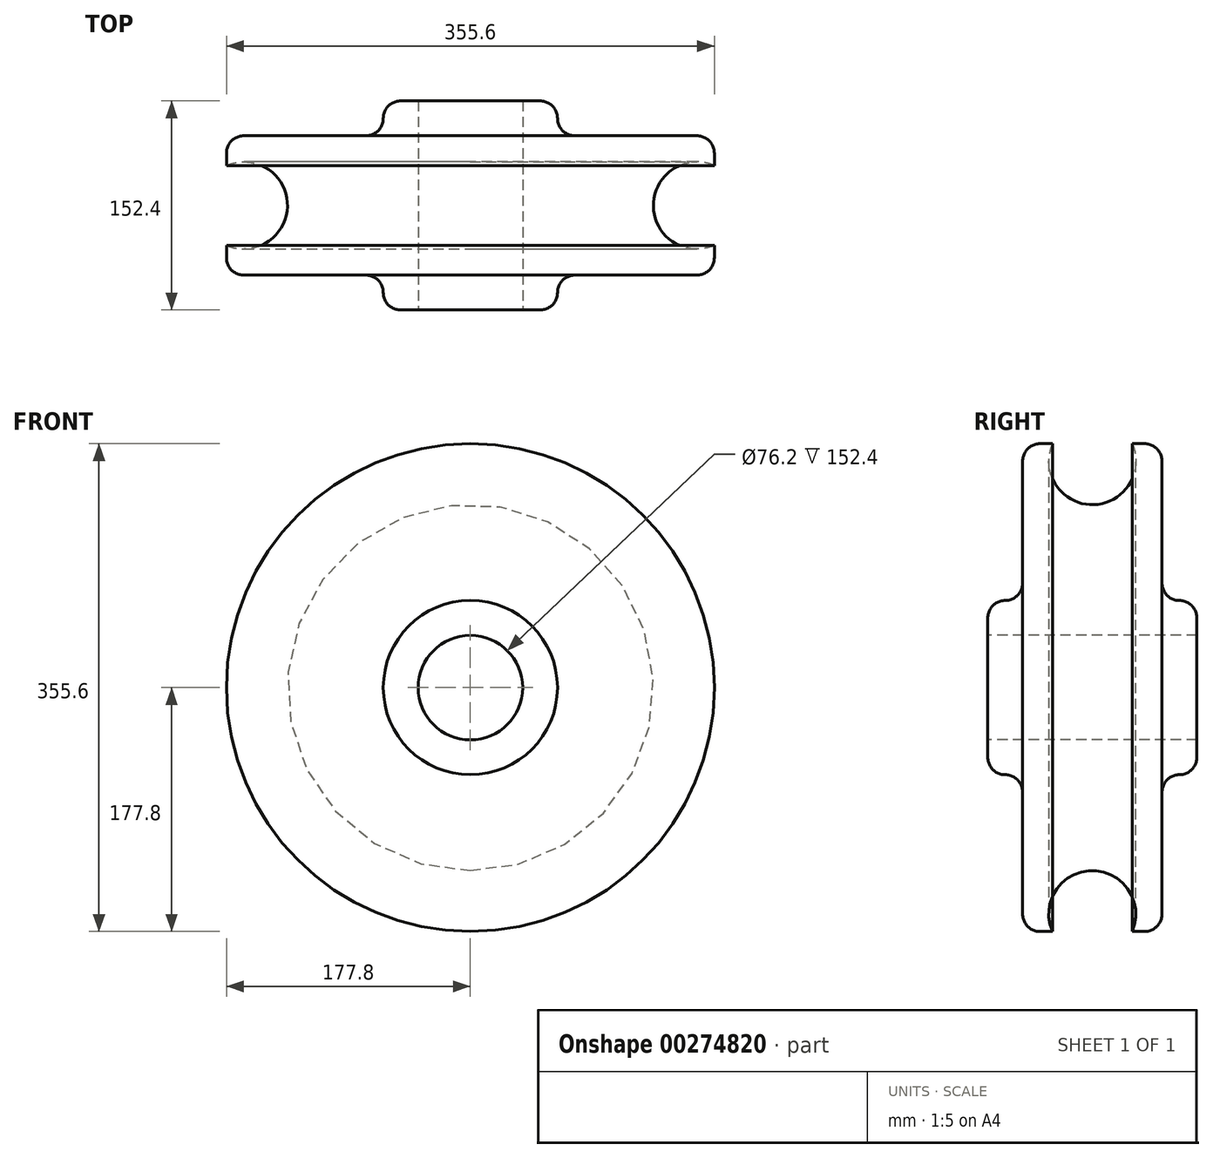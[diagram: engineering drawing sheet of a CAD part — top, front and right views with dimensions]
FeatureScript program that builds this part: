
annotation { "Feature Type Name" : "Feature", "Feature Type Description" : "" }
export const myFeature = defineFeature(function(context is Context, id is Id, definition is map)
    precondition{}
    {
        {
            var Q0;
            Q0=qCreatedBy(makeId("Right.planeOp"),FACE);
            var sketch = newSketch(context, id + "F0", { "sketchPlane" : qUnion([Q0])});
            skLineSegment(sketch, "E0.bottom", {"start": v(76.2, 63.5) * mm, "end": v(-76.2, 63.5) * mm});
            skPoint(sketch, "E0.middle", {"position": v(0, 0) * mm});
            skLineSegment(sketch, "E1.bottom", {"start": v(50.8, 177.8) * mm, "end": v(29.1, 177.8) * mm});
            skLineSegment(sketch, "E1.left", {"start": v(50.8, 177.8) * mm, "end": v(50.8, 63.5) * mm});
            skLineSegment(sketch, "E1.right", {"start": v(-50.8, 177.8) * mm, "end": v(-50.8, 63.5) * mm});
            skArc(sketch, "E2", {"start": v(-29.1, 177.8) * mm, "mid": v(0, 133.35) * mm, "end": v(29.1, 177.8) * mm});
            skLineSegment(sketch, "E3.top", {"start": v(76.2, 38.1) * mm, "end": v(-76.2, 38.1) * mm});
            skLineSegment(sketch, "E4.trimOffspring", {"start": v(-29.1, 177.8) * mm, "end": v(-50.8, 177.8) * mm});
            skLineSegment(sketch, "E5.bottom", {"start": v(-76.2, 38.1) * mm, "end": v(76.2, 38.1) * mm, "construction": true});
            skLineSegment(sketch, "E6", {"start": v(-76.2, 63.5) * mm, "end": v(-76.2, 38.1) * mm});
            skLineSegment(sketch, "E7", {"start": v(76.2, 63.5) * mm, "end": v(76.2, 38.1) * mm});
            skLineSegment(sketch, "E8.top", {"start": v(-76.2, 0) * mm, "end": v(76.2, 0) * mm, "construction": true});
            skLineSegment(sketch, "E8.left", {"start": v(-76.2, 38.1) * mm, "end": v(-76.2, 0) * mm, "construction": true});
            skLineSegment(sketch, "E8.right", {"start": v(76.2, 38.1) * mm, "end": v(76.2, 0) * mm, "construction": true});
            skSolve(sketch);
        }
        {
            var Q0;
            Q0=makeQuery(id+"F0.imprint","IMPRINT",FACE,{"disambiguationData":[TD([[makeQuery(id+"F0.imprint","IMPRINT",EDGE,{"derivedFrom":sQuery(id+"F0.wireOp",EDGE,"E1.bottom")}),1.0]])]});
            var Q1;
            Q1=makeQuery(id+"F0.imprint","IMPRINT",FACE,{"disambiguationData":[TD([[makeQuery(id+"F0.imprint","IMPRINT",EDGE,{"derivedFrom":sQuery(id+"F0.wireOp",EDGE,"E3.top")}),-1.0]])]});
            var Q2;
            Q2=sQuery(id+"F0.wireOp",EDGE,"E8.top");
            revolve(context, id + "F1", {"entities" : qUnion([Q0, Q1]), "axis" : qUnion([Q2]), "revolveType" : RevolveType.FULL});
        }
        {
            var Q0;
            Q0=makeQuery(id+"F1.opRevolve","SWEPT_EDGE",EDGE,{"disambiguationData":[OSD([sQuery(id+"F0.wireOp",EDGE,"E1.right"),sQuery(id+"F0.wireOp",EDGE,"E4.trimOffspring")])]});
            var Q1;
            Q1=makeQuery(id+"F1.opRevolve","SWEPT_EDGE",EDGE,{"disambiguationData":[OSD([sQuery(id+"F0.wireOp",EDGE,"E1.bottom"),sQuery(id+"F0.wireOp",EDGE,"E1.left")])]});
            var Q2;
            Q2=makeQuery(id+"F1.opRevolve","SWEPT_EDGE",EDGE,{"disambiguationData":[OSD([sQuery(id+"F0.wireOp",EDGE,"E0.bottom"),sQuery(id+"F0.wireOp",EDGE,"E6")])]});
            var Q3;
            Q3=makeQuery(id+"F1.opRevolve","SWEPT_EDGE",EDGE,{"disambiguationData":[OSD([sQuery(id+"F0.wireOp",EDGE,"E0.bottom"),sQuery(id+"F0.wireOp",EDGE,"E7")])]});
            var Q4;
            Q4=makeQuery(id+"F1.opRevolve","SWEPT_EDGE",EDGE,{"disambiguationData":[OSD([sQuery(id+"F0.wireOp",EDGE,"E0.bottom"),sQuery(id+"F0.wireOp",EDGE,"E1.right")])]});
            var Q5;
            Q5=makeQuery(id+"F1.opRevolve","SWEPT_EDGE",EDGE,{"disambiguationData":[OSD([sQuery(id+"F0.wireOp",EDGE,"E0.bottom"),sQuery(id+"F0.wireOp",EDGE,"E1.left")])]});
            fillet(context, id + "F2", {"entities" : qUnion([Q0, Q1, Q2, Q3, Q4, Q5]), "radius" : 12.7 * mm, "tangentPropagation" : true, "allowEdgeOverflow" : false});
        }
    });
